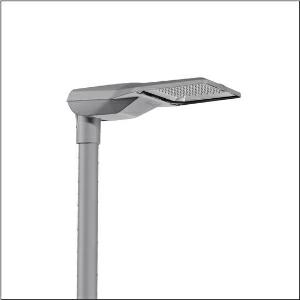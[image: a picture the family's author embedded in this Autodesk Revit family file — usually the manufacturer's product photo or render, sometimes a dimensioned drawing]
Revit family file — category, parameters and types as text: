
# Revit family: streetlight_sl_21_iq_midi___stw1_0a_5xe3e41d08mb_aeb4
name_source: partatom
category: Lighting Fixtures
units: mm (PartAtom-declared; Revit-internal decimal feet)

## family parameters
Cut with Voids When Loaded = No
Host = Face
Light Source = No
Part Type = Normal
Room Calculation Point = No
Round Connector Dimension = Use Diameter
Shared = No

## types (1)
- --- (1 x LED, 20360 lm, 146.7 W, 4000K)
    Apparent Load = 147 VA
    CIE Flux Codes = 38 75 98 100 100
    Color Rendering = 70
    Color Temperature = 4000K
    Default Elevation = 1800 mm
    Description = Streetlight SL 21 iQ midi, mast luminaire, primary light control with lens, of PMMA, primary optical cover: cover, of toughened safety glass, transparent, light distribution: STW1.0a, light emission: direct distribution, primary light characteristic: asymmetric, installation type: post-top, side-entry, LED, High Power LED, rated luminous flux: 20.360lm, luminous efficacy: 139lm/W, light colour: 740, colour temperature: 4000K, control: Auto-Match, Temp-Guard, Lumen-Switch, Night-Set, Smart-Wire, Light-Fading, Desk-Remote (wireless, voltage-free reading and setting of iQ features in the workshop via application-optimized NFC function/RFID function), optimised constant luminous flux control (CLO 2.0), pre-setting: linear dimming characteristic, mains connection: 230..240V, AC, 50/60Hz, start of lifetime: 147W, end of service life: 161W, reduction: 62W, luminaire housing, of diecast aluminium, powder-coated, Siteco® metallic grey (DB 702S), corrosivity category C5 mid according to DIN EN ISO 12944, please order mast flange separately, inclination adjustable: 0°, 5°, 10°, 15°, sealing non-destructively replaceable, multi-level sealing system, length: 644mm, width: 335mm, height: 110mm, mast flange for spigot size: 42mm (side-entry): 5XC10008XM4, 60/48mm (side-entry/post-top): 5XC10108XM2, 76/60mm (side-entry/post-top): 5XC10108XM1, protection rating (complete): IP66, insulation class (complete): insulation class II (safety insulation), certification: CE, ENEC, ENEC+, VDE, impact resistance: IK09, permissible operating ambient temperature for outdoor applications: -40..+50°C, standard-compliant lighting for roads and squares, packaging unit: 1 piece

Light Distribution: STW1.0a
    Height = 111 mm
    Lamp = 1 x LED
    Lamp Light Flux = 20360 lm
    Lamp Power = 146.7 W
    Lamp count = 1
    Length = 644 mm
    Luminous efficacy = 139 lm/W
    Manufacturer = Siteco
    ModVariant = No
    Model = 5XE3E41D08MB
    Number of Poles = 1
    OnlyDefault = Yes
    Power Factor = 1
    Product Name = Streetlight SL 21 iQ midi | STW1.0a
    Product group = mast luminaire | pylon top
    ProductGroupID = 6100
    Protection Class = Protection class II
    Protection Degree = IP 66
    RLX_Detail_Level = 1
    RLX_Emergency_Light_Flux = 0 lm
    RLX_Emergency_Type = 0
    RLX_Emergency_Type_DB = No
    RlxData = <blob elided: 90713 chars, md5=a6255f9c>
    Socket = socket
    Standby Power = 0 W
    System Light Flux = 20360 lm
    System Power = 147 W
    Type Comments = factory setting: luminous flux: 100 % | dim-lin: 254 | 753 mA
    Type Image = l_1004298.jpg
    URL = http://relux.com
    VarID = @adj_160175
    Voltage = 0 V
    Weight = 0.00 kg
    Width = 336 mm

## geometry (parser evidence)
native form markers: Blend x4, Sweep x10
no freeform markers — native parametric forms only
